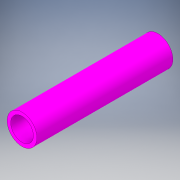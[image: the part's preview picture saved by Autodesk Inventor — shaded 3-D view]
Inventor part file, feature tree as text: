
AUTODESK INVENTOR PART (.ipt)
format: ipt  version: 2018 (Build 220112000, 112)  size: 108,544 bytes
history: native  units: in
note: dims shown in document units (in); Inventor stores cm internally (conversion verified against a paired STEP export)
features: extrude x1, sketch x1
ambient origin geometry x8: Origin, YZ Plane, XZ Plane, XY Plane, X Axis, Y Axis, Z Axis, Center Point
bodies: Solid1 (feature_tree)
feature tree (2):
  extrude  "Extrusion1"  Depth=6.0in
  sketch  "Sketch1"  dims[d0=1.315in d1=1.0in d2=6.0in d3=0.0in]
